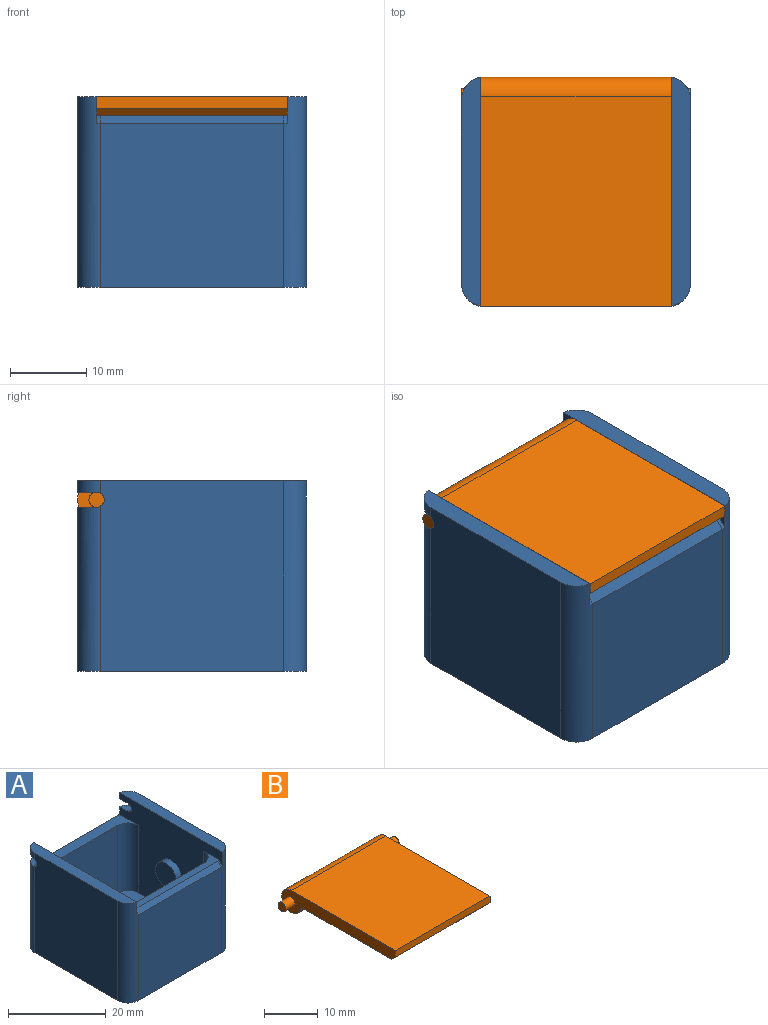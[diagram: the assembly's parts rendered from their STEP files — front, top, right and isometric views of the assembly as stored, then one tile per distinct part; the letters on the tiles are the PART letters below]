
ASSEMBLY  parts=2 mates=1
PART A: 37 faces, bbox 30x30x25 mm
  f0: plane 19x17mm, normal (0,-1,0), area 323mm2, adj f13,f19,f20,f21
  f1: plane 29.96x2.5mm, normal (0,0,1), area 71.3mm2, adj f7,f10,f25,f26
  f2: plane 2.46x2.46mm, normal (0,0,1), area 4.3mm2, adj f7,f17,f23
  f3: plane 2.5x2.47mm, normal (0,0,-1), area 4.4mm2, adj f7,f17,f25
  f4: plane 24x19.5mm, normal (0,1,0), area 468mm2, adj f12,f19,f22,f23
  f5: plane 20x19mm, normal (0,1,0), area 380mm2, adj f13,f14,f28,f29
  f6: plane 24x21.5mm, normal (0,-1,0), area 516mm2, adj f12,f26,f27,f31
  f7: plane 30x22.54mm, normal (1,0,0), area 465.2mm2, adj f1,f2,f3,f13,f14,f17,f19,f20
  f8: plane 30x22.54mm, normal (-1,0,0), area 437mm2, adj f11,f13,f14,f15,f16,f18,f19,f21
  f9: plane 25x24.04mm, normal (1,0,0), area 579.8mm2, adj f11,f12,f15,f22,f24,f27,f35
  f10: plane 25x24.04mm, normal (-1,0,0), area 599.5mm2, adj f1,f12,f17,f23,f25,f26
  f11: plane 29.96x2.5mm, normal (0,0,1), area 71.3mm2, adj f8,f9,f24,f27
  f12: plane 30x30mm, normal (0,0,-1), area 892.3mm2, adj f4,f6,f9,f10,f22,f23,f26,f27
  f13: plane 25x25mm, normal (0,0,1), area 617.3mm2, adj f0,f5,f7,f8,f20,f21,f28,f29
  f14: plane 25x4.5mm, normal (0,0,1), area 41.3mm2, adj f5,f7,f8,f28,f29,f30,f31,f32
  f15: cylinder r=1mm len=2.5mm, axis (-1,0,0), area 7.8mm2, adj f8,f9,f16,f18,f22,f24
  f16: plane 2.46x2.46mm, normal (0,0,1), area 4.3mm2, adj f8,f15,f22
  f17: cylinder r=1mm len=2.5mm, axis (-1,0,0), area 7.8mm2, adj f2,f3,f7,f10,f23,f25
  f18: plane 2.5x2.47mm, normal (0,0,-1), area 4.4mm2, adj f8,f15,f24
  f19: plane 25x5.5mm, normal (0,0,1), area 66.3mm2, adj f0,f4,f7,f8,f20,f21,f22,f23
  f20: cylinder r=3mm len=17mm, axis (0,0,1), area 80.1mm2, adj f0,f7,f13,f19
  f21: cylinder r=3mm len=17mm, axis (0,0,-1), area 80.1mm2, adj f0,f8,f13,f19
  f22: cylinder r=3mm len=21.63mm, axis (0,0,1), area 100.3mm2, adj f4,f8,f9,f12,f15,f16,f19
  f23: cylinder r=3mm len=21.63mm, axis (0,0,-1), area 100.3mm2, adj f2,f4,f7,f10,f12,f17,f19
  f24: cylinder r=3mm len=2.96mm, axis (0,0,1), area 6.3mm2, adj f8,f9,f11,f15,f18
  f25: cylinder r=3mm len=2.96mm, axis (0,0,1), area 6.3mm2, adj f1,f3,f7,f10,f17
  f26: cylinder r=3mm len=25mm, axis (0,0,1), area 116.1mm2, adj f1,f6,f7,f10,f12,f30
  f27: cylinder r=3mm len=25mm, axis (0,0,-1), area 116.1mm2, adj f6,f8,f9,f11,f12,f32
  f28: cylinder r=3mm len=20mm, axis (0,0,1), area 94.2mm2, adj f5,f8,f13,f14
  f29: cylinder r=3mm len=20mm, axis (0,0,-1), area 94.2mm2, adj f5,f7,f13,f14
  f30: cone r=2mm half-angle=45deg, axis (0,0,-1), area 0.7mm2, adj f7,f14,f26,f31
  f31: plane 24x1mm, normal (0,-0.71,0.71), area 33.9mm2, adj f6,f14,f30,f32
  f32: cone r=2mm half-angle=45deg, axis (0,0,-1), area 0.7mm2, adj f8,f14,f27,f31
  f33: cylinder r=3mm len=6mm, axis (1,0,0), area 28.3mm2, adj f8,f34
  f34: plane 6x6mm, normal (-1,0,0), area 28.3mm2, adj f33
  f35: cylinder r=2.5mm len=5mm, axis (1,0,0), area 47.1mm2, adj f9,f36
  f36: plane 5x5mm, normal (1,0,0), area 19.6mm2, adj f35
PART B: 11 faces, bbox 30x30x5 mm
  f0: plane 25x24mm, normal (0,0,-1), area 600mm2, adj f1,f4,f5,f10
  f1: cylinder r=2.5mm len=25mm, axis (-1,0,0), area 294.5mm2, adj f0,f2,f4,f5
  f2: plane 27.5x25mm, normal (0,0,1), area 687.5mm2, adj f1,f3,f4,f5
  f3: plane 25x1.5mm, normal (0,-1,0), area 37.5mm2, adj f2,f4,f5,f10
  f4: plane 30x5mm, normal (1,0,0), area 79.8mm2, adj f0,f1,f2,f3,f8,f10
  f5: plane 30x5mm, normal (-1,0,0), area 79.8mm2, adj f0,f1,f2,f3,f7,f10
  f6: plane 2x2mm, normal (-1,0,0), area 3.1mm2, adj f7
  f7: cylinder r=1mm len=2.5mm, axis (-1,0,0), area 15.7mm2, adj f5,f6
  f8: cylinder r=1mm len=2.5mm, axis (-1,0,0), area 15.7mm2, adj f4,f9
  f9: plane 2x2mm, normal (1,0,0), area 3.1mm2, adj f8
  f10: plane 25x1mm, normal (0,-0.71,-0.71), area 35.4mm2, adj f0,f3,f4,f5
PLACE A t=(0,-4.16,0)mm
PLACE B t=(0,-40.46,-9.25)mm
MATE fastened B.f1 <-> A.f15  axis (-1,0,0) through (-15,8.34,22.5)mm
